# Revit family: HVAC_Heaters_Enertech_CTC-GS-600
name_source: partatom
category: Specialty Equipment
revit_build: Autodesk Revit 2017 (Build: 20190508_0315(x64)
units: mm (PartAtom-declared; Revit-internal decimal feet)

## family parameters
Always vertical = Yes
Cut with Voids When Loaded = No
OmniClass Number = 23.75.00.00
OmniClass Title = Climate Control (HVAC)
Part Type = Normal
Room Calculation Point = No
Round Connector Dimension = Use Diameter
Shared = No
Work Plane-Based = No

## types (6) — shared parameters
AssetType = Fixed
BIMObjectName = HVAC_Heaters_Enertech_CTC-GS-600
Brand = CTC
BrineSystem_Min_MaxPressure = 0.2 - 3 bar
CO2Equivalent = 3.371 tonnes
Capacity = Fixed
Category = Heat pumps, Geothermal
Color = white
DurationUnit = Year
EnergyClassHeatingWithControl = A+++/A++
EnergyClassHeatingWithoutControl = A++/A++
EnergyClass_HotWater_TapProfile = A/XL
HasProtectiveEarth = Yes
HotTapWaterPerformance = 210 - 304 liter
IP_Code = IP X1
IfcExportAs = IfcElectricalDeviceCommon
IfcExportType = HEATER
Manufacturer = Enertech AB
ManufacturerCountry = Sweden
ManufacturerName = Enertech AB
ManufacturerURL = https://ctc.se
Material = Steel/copper
MaxOperatingPressureHotWater = 10 bar
MaxOperatingPressureThermalStore = 3 bar
MinimumCeilingHeight = 1940 mm
NBSDescription = Air to water heat pumps
NBSReference = 90-40-40/320
Name = CTC-GS-600
NominalCurrent = 0 A
NominalDepth = 673 mm  [stored 2.20801 ft]
NominalFrequencyRange = 50 Hz
NominalHeight = 1876 mm
NominalWidth = 596 mm  [stored 1.95538 ft]
PhaseAngle = 0.00°
PowerFactor = 0 W
ProductInformation = Price-worthy, quiet on/off geothermal heat pumps with control touchscreen and hot water preparation. Model: 6 and 8, 6-8 kW, 230V-400V.
PumpMainMaterial = Stainless Steel
PumpSecondaryMaterial = Plastic, Opaque Black
PumpTertiaryMaterial = Copper
RefrigerantQuantity = 1.9 kg
RefrigerantType = R407C
Shape = Rectanular
Touchscreen = yes
UNSPSCCode = 40101806
URL = https://ctc-heating.com
Uniclass2 = Pr_40_70_65
Uniclass2015Description = Preparation catering equipment
Uniclass2015Reference = Pr_40_70_65
UsageCurrent = 0 A
Version = 1
VersionDate = 09/12/2020
WarrantyDurationUnit = Year
WaterVolumeHeathingSystem = 229 liter
WaterVolumeWaterSuply = 1.7 liter
zero-valued in all types: Cost

## per-type parameters (varying)
| type | COP | ConvergoRefNr | Description | EANNumber | ElectricalDeviceNominalPower | GroupFuse | InPutPower | MaxStartingCurrent | Model | ModelNumber | NominalVoltage | NumberOfPoles | OutputRangeIimmersionHeater | RatedCurrent | RatedHeatOutputModerate | RatedVoltage | SCOPCold | SCOPModerate | SCOPWarm | Size | Sound pressureLPA 1m | SoundPowerLWA | SpecifiedOutput | Weight |
| CTC GS 606 - 400V3N | 4.52 | 0091-1710-0008-SE | Price-worthy, quiet on/off geothermal heat pumps with control touchscreen and hot water preparation. Model: 6 and 8, 6-8 kW, 230V-400V. | 7333077094355 | 9000 W | 20 A | 1.34 kW | 16.6 A | CTC GS 606 | 589310001 | 400 V | 3 | 0.3 - 9 kW | 17 A | 7 kW | 1200 V | 4.80 | 4.72 | 4.64 | 673x596x1876 mm | 36 dB(A) | 41 dB(A) | 6.0 kW | 250 kg |
| CTC GS 606 - 230V1N | 4.52 | 0091-1710-0008-SE | Price-worthy, quiet on/off geothermal heat pumps with control touchscreen and hot water preparation. Model: 6 and 8, 6-8 kW, 230V-400V. | 7333077094379 | 5500 W | 50 A | 1.34 kW | 18.09 A | CTC GS 606 | 589311001 | 230 V | 1 | 0.3 - 5.5 kW | 38 A | 7 kW | 230 V | 4.80 | 4.72 | 4.64 | 673x596x1876 mm | 36 dB(A) | 41 dB(A) | 6.0 kW | 256 kg |
| CTC GS 606 - 230V3N | 4.52 | 0091-1710-0008-SE | Price-worthy, quiet on/off geothermal heat pumps with control touchscreen and hot water preparation. Model: 6 and 8, 6-8 kW, 230V-400V. | 7333077094393 | 7000 W | 35 A | 1.34 kW | 18.09 A | CTC GS 606 | 589312001 | 230 V | 3 | 1.2 - 7 kW | 30 A | 7 kW | 690 V | 4.80 | 4.72 | 4.64 | 673x596x1876 mm | 36 dB(A) | 41 dB(A) | 6.0 kW | 256 kg |
| CTC GS 608 - 400V3N | 4.77 | 0091-1710-0009-SE | Price-worthy, quiet on/off geothermal heat pumps with control touchscreen and hot water preparation. Model: 6 and 8, 6-8 kW, 230V-400V. | 7333077094362 | 9000 W | 25 A | 1.74 kW | 17.7 A | CTC GS 608 | 589310002 | 400 V | 3 | 0.3 - 9 kW | 19 A | 9 kW | 1200 V | 5.04 | 4.96 | 4.90 | 673x596x1882 mm | 34 dB(A) | 39 dB(A) | 8.3 kW | 246 kg |
| CTC GS 608 - 230V1N | 4.77 | 0091-1710-0009-SE |  | 7333077094386 | 5500 W | 50 A | 1.74 kW | 21.4 A | CTC GS 608 | 589311002 | 230 V | 1 | 0.3 - 5.5 kW | 43 A | 9 kW | 230 V | 5.04 | 4.96 | 4.90 | 673x596x1882 mm | 34 dB(A) | 39 dB(A) | 8.3 kW | 254 kg |
| CTC GS 608 - 230V3N | 4.77 | 0091-1710-0009-SE |  | 7333077094409 | 7000 W | 50 A | 1.74 kW | 21.4 A | CTC GS 608 | 589312002 | 230 V | 3 | 1.2 - 7 kW | 34 A | 9 kW | 690 V | 5.04 | 4.96 | 4.90 | 673x596x1882 mm | 34 dB(A) | 39 dB(A) | 8.3 kW | 254 kg |

note: [stored X ft] marks values corroborated as IEEE doubles in the binary element streams (Revit-internal decimal feet)

## geometry (parser evidence)
native form markers: Sweep x5
no freeform markers — native parametric forms only
